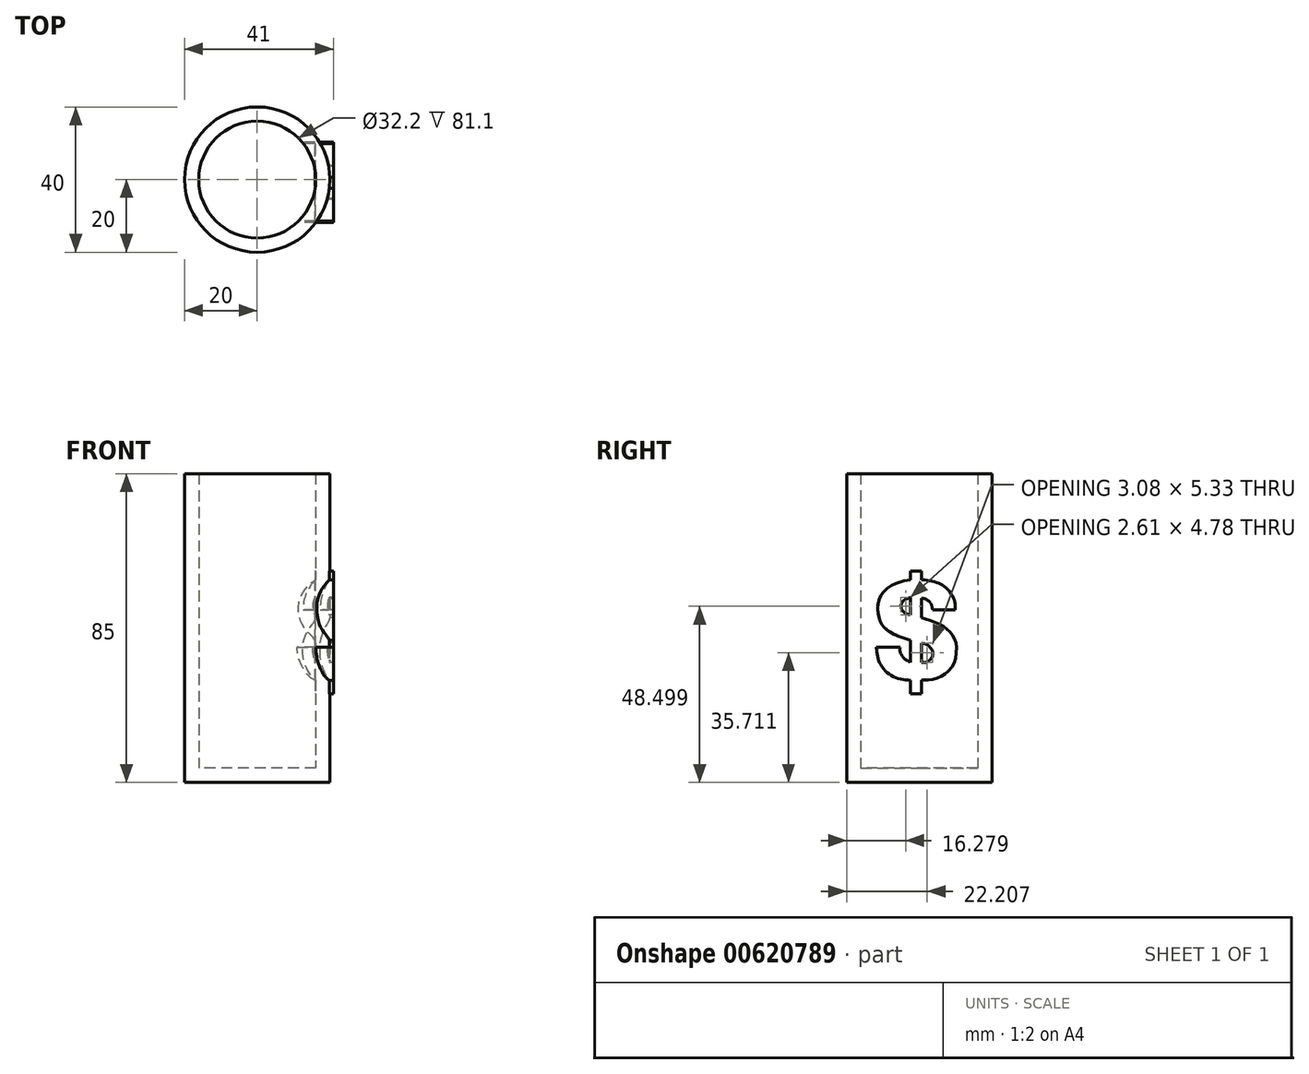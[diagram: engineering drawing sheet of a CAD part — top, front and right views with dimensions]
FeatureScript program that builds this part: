
annotation { "Feature Type Name" : "Feature", "Feature Type Description" : "" }
export const myFeature = defineFeature(function(context is Context, id is Id, definition is map)
    precondition{}
    {
        {
            var Q0;
            Q0=qCreatedBy(makeId("Top.planeOp"),FACE);
            var sketch = newSketch(context, id + "F0", { "sketchPlane" : qUnion([Q0])});
            skCircle(sketch, "E0", {"center": v(0, 0) * mm, "radius": 20 * mm});
            skSolve(sketch);
        }
        {
            var Q0;
            Q0=qSketchRegion(id+"F0",true);
            extrude(context, id + "F1", {"entities" : qUnion([Q0]), "depth" : 85 * mm, "offsetDistance" : 25.4 * mm});
        }
        {
            var Q0;
            Q0=makeQuery(id+"F1.opExtrude","CAP_FACE",FACE,{"disambiguationData":[OSD([sQuery(id+"F0.wireOp",EDGE,"E0")])],"isStart":false});
            shell(context, id + "F2", {"entities" : qUnion([Q0]), "thickness" : 3.9 * mm});
        }
        {
            var Q0;
            Q0=qCreatedBy(makeId("Right.planeOp"),FACE);
            var sketch = newSketch(context, id + "F3", { "sketchPlane" : qUnion([Q0])});
            skLineSegment(sketch, "E1", {"start": v(-11.81, 37.21) * mm, "end": v(-5.28, 37.21) * mm});
            skFitSpline(sketch, "E2", {"points": [v(-5.28, 37.21) * mm, v(-5.28, 35.96) * mm, v(-4.74, 34.93) * mm, v(-3.98, 33.94) * mm, v(-3.22, 33.5) * mm, v(-2.41, 33.05) * mm], "startDerivative": vector(-0.65, -6.08) * mm, "endDerivative": vector(4.38, -2.55) * mm});
            skLineSegment(sketch, "E3", {"start": v(-2.41, 33.05) * mm, "end": v(-2.41, 39.1) * mm});
            skFitSpline(sketch, "E4", {"points": [v(-2.41, 39.1) * mm, v(-5.82, 40.3) * mm, v(-8.9, 42) * mm, v(-10.52, 43.88) * mm, v(-11.37, 46.97) * mm, v(-10.96, 50.69) * mm, v(-8.23, 53.86) * mm, v(-4.52, 55.39) * mm, v(-2.41, 55.79) * mm], "startDerivative": vector(-26.11, 8.4) * mm, "endDerivative": vector(19.36, 3) * mm});
            skLineSegment(sketch, "E5", {"start": v(-2.41, 55.79) * mm, "end": v(-2.41, 58.16) * mm});
            skLineSegment(sketch, "E6", {"start": v(-2.41, 58.16) * mm, "end": v(0.58, 58.16) * mm});
            skLineSegment(sketch, "E7", {"start": v(0.58, 58.16) * mm, "end": v(0.58, 55.79) * mm});
            skFitSpline(sketch, "E8", {"points": [v(0.58, 55.79) * mm, v(1.35, 55.79) * mm, v(2.96, 55.54) * mm, v(4.66, 55.06) * mm, v(5.8, 54.6) * mm, v(7.05, 53.85) * mm, v(8.4, 52.53) * mm, v(9.28, 51.1) * mm, v(9.72, 49.94) * mm, v(9.9, 48.7) * mm, v(9.93, 47.58) * mm], "startDerivative": vector(9.3, 0.4) * mm, "endDerivative": vector(0.12, -12.25) * mm});
            skLineSegment(sketch, "E9", {"start": v(9.93, 47.58) * mm, "end": v(3.64, 47.58) * mm});
            skFitSpline(sketch, "E10", {"points": [v(3.64, 47.58) * mm, v(3.48, 48.53) * mm, v(3, 49.57) * mm, v(2.03, 50.33) * mm, v(1.13, 50.66) * mm, v(0.67, 50.66) * mm], "startDerivative": vector(-0.54, 4.59) * mm, "endDerivative": vector(-3.02, -0.29) * mm});
            skLineSegment(sketch, "E11", {"start": v(0.67, 50.66) * mm, "end": v(0.67, 45.4) * mm});
            skFitSpline(sketch, "E12", {"points": [v(0.67, 45.4) * mm, v(2.41, 44.81) * mm, v(4.72, 43.9) * mm, v(6.52, 43.06) * mm, v(8.02, 41.84) * mm, v(9.04, 40.72) * mm, v(9.9, 39.09) * mm, v(10.27, 37.68) * mm, v(10.1, 34.73) * mm, v(9.54, 32.7) * mm, v(8.06, 30.7) * mm, v(6.68, 29.59) * mm, v(4.85, 28.75) * mm, v(2.87, 28.25) * mm, v(1.65, 28.2) * mm, v(0.67, 28.14) * mm], "startDerivative": vector(25.33, -8) * mm, "endDerivative": vector(-20.13, -1.48) * mm});
            skLineSegment(sketch, "E13", {"start": v(0.67, 28.14) * mm, "end": v(0.67, 24.36) * mm});
            skLineSegment(sketch, "E14", {"start": v(0.67, 24.36) * mm, "end": v(-2.37, 24.36) * mm});
            skLineSegment(sketch, "E15", {"start": v(-2.37, 24.36) * mm, "end": v(-2.37, 28.14) * mm});
            skFitSpline(sketch, "E16", {"points": [v(-2.37, 28.14) * mm, v(-4.96, 28.43) * mm, v(-7.4, 29.24) * mm, v(-9.5, 30.9) * mm, v(-10.88, 32.92) * mm, v(-11.52, 34.82) * mm, v(-11.76, 36.77) * mm, v(-11.81, 37.21) * mm], "startDerivative": vector(-16.02, 1.23) * mm, "endDerivative": vector(-0.83, 5.25) * mm});
            skLineSegment(sketch, "E17", {"start": v(0.67, 38.37) * mm, "end": v(0.67, 33.09) * mm});
            skFitSpline(sketch, "E18", {"points": [v(0.67, 38.37) * mm, v(1.5, 38.18) * mm, v(2.61, 37.6) * mm, v(3.36, 36.8) * mm, v(3.72, 36.06) * mm, v(3.72, 35.14) * mm, v(3.52, 34.44) * mm, v(2.82, 33.69) * mm, v(2.08, 33.2) * mm, v(1.42, 33) * mm, v(0.67, 33.09) * mm], "startDerivative": vector(8.13, -1.47) * mm, "endDerivative": vector(-8.36, 1.56) * mm});
            skLineSegment(sketch, "E19", {"start": v(-2.41, 46.1) * mm, "end": v(-2.41, 50.89) * mm});
            skFitSpline(sketch, "E20", {"points": [v(-2.41, 50.89) * mm, v(-3.7, 50.45) * mm, v(-4.7, 49.65) * mm, v(-5.02, 48.39) * mm, v(-4.42, 47.06) * mm, v(-3.47, 46.43) * mm, v(-2.41, 46.1) * mm], "startDerivative": vector(-7.6, -2.18) * mm, "endDerivative": vector(6.91, -1.74) * mm});
            skSolve(sketch);
        }
        {
            var Q0;
            Q0 = qSketchRegion(id + "F3", true);
            extrude(context, id + "F4", {"entities" : qUnion([Q0]), "operationType" : NewBodyOperationType.ADD, "depth" : 21 * mm, "offsetDistance" : 25 * mm});
        }
        {
            var Q0;
            Q0 = qSketchRegion(id + "F3", true);
            extrude(context, id + "F5", {"entities" : qUnion([Q0]), "operationType" : NewBodyOperationType.REMOVE, "depth" : 16 * mm, "offsetDistance" : 25 * mm});
        }
    });
